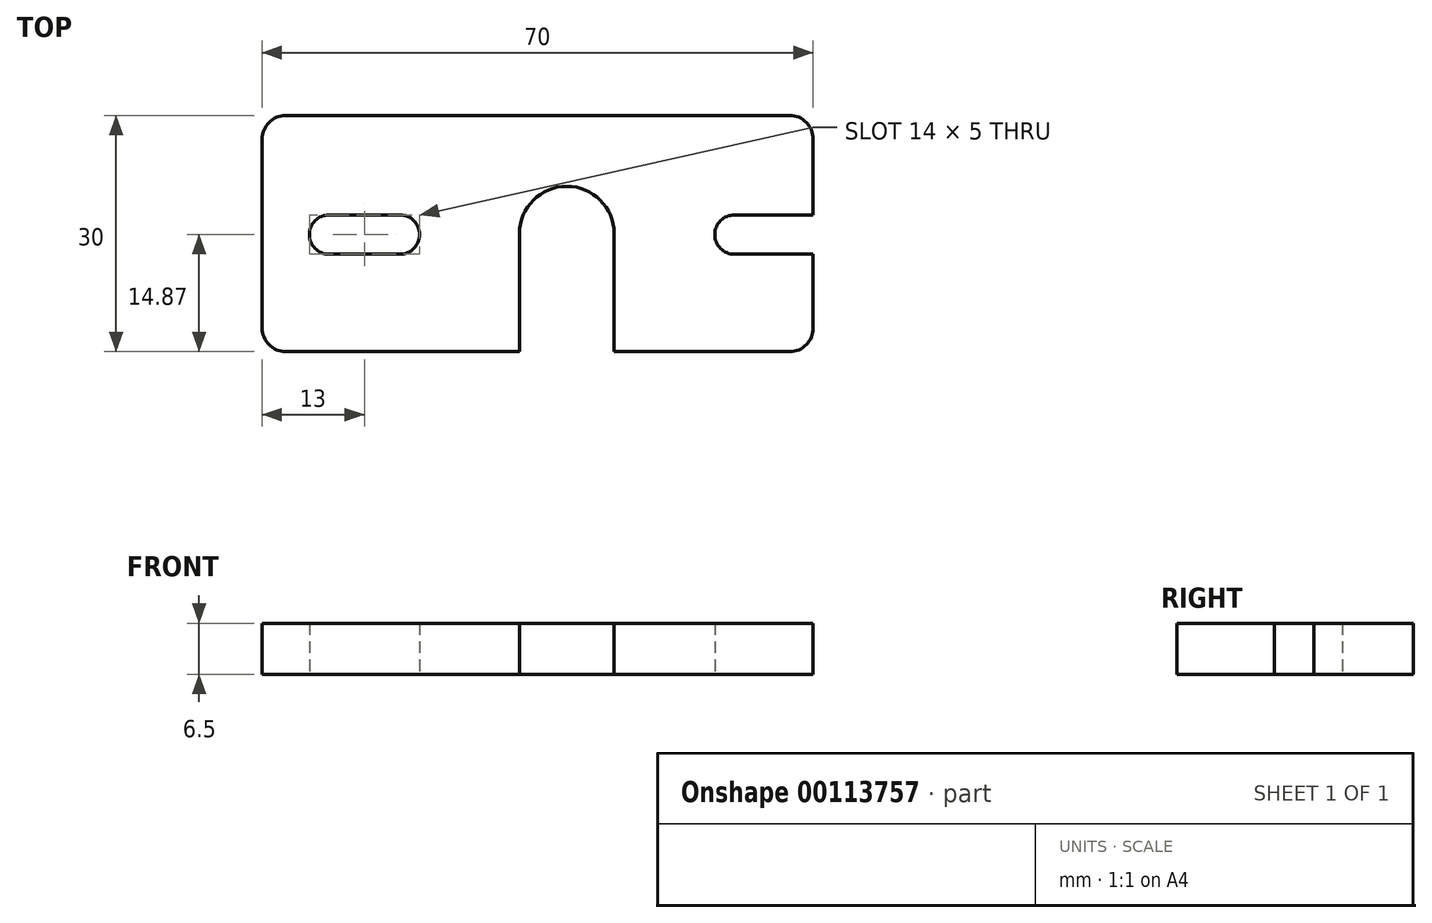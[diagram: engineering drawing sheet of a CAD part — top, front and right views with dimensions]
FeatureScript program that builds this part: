
annotation { "Feature Type Name" : "Feature", "Feature Type Description" : "" }
export const myFeature = defineFeature(function(context is Context, id is Id, definition is map)
    precondition{}
    {
        {
            var Q0;
            Q0=qCreatedBy(makeId("Top.planeOp"),FACE);
            var sketch = newSketch(context, id + "F0", { "sketchPlane" : qUnion([Q0])});
            skLineSegment(sketch, "E0.bottom", {"start": v(-35.7, 15.13) * mm, "end": v(28.3, 15.13) * mm});
            skLineSegment(sketch, "E0.top", {"start": v(-35.7, -14.87) * mm, "end": v(28.3, -14.87) * mm});
            skLineSegment(sketch, "E0.left", {"start": v(-38.7, 12.13) * mm, "end": v(-38.7, -11.87) * mm});
            skLineSegment(sketch, "E0.right", {"start": v(31.3, 12.13) * mm, "end": v(31.3, -11.87) * mm});
            skLineSegment(sketch, "E1.bottom", {"start": v(6, -14.87) * mm, "end": v(-6, -14.87) * mm});
            skLineSegment(sketch, "E1.top", {"start": v(6, 0.13) * mm, "end": v(-6, 0.13) * mm});
            skLineSegment(sketch, "E1.left", {"start": v(6, -14.87) * mm, "end": v(6, 0.13) * mm});
            skLineSegment(sketch, "E1.right", {"start": v(-6, -14.87) * mm, "end": v(-6, 0.13) * mm});
            skArc(sketch, "E2", {"start": v(6, 0.13) * mm, "mid": v(0, 6.13) * mm, "end": v(-6, 0.13) * mm});
            skPoint(sketch, "E3.visualSharp", {"position": v(-38.7, 15.13) * mm});
            skArc(sketch, "E3.filletArc", {"start": v(-35.7, 15.13) * mm, "mid": v(-37.82, 14.25) * mm, "end": v(-38.7, 12.13) * mm});
            skPoint(sketch, "E4.visualSharp", {"position": v(31.3, 15.13) * mm});
            skArc(sketch, "E4.filletArc", {"start": v(31.3, 12.13) * mm, "mid": v(30.42, 14.25) * mm, "end": v(28.3, 15.13) * mm});
            skPoint(sketch, "E5.visualSharp", {"position": v(31.3, -14.87) * mm});
            skArc(sketch, "E5.filletArc", {"start": v(28.3, -14.87) * mm, "mid": v(30.42, -13.99) * mm, "end": v(31.3, -11.87) * mm});
            skPoint(sketch, "E6.visualSharp", {"position": v(-38.7, -14.87) * mm});
            skArc(sketch, "E6.filletArc", {"start": v(-38.7, -11.87) * mm, "mid": v(-37.82, -13.99) * mm, "end": v(-35.7, -14.87) * mm});
            skLineSegment(sketch, "E7.bottom", {"start": v(21.3, 2.5) * mm, "end": v(31.3, 2.5) * mm});
            skLineSegment(sketch, "E7.top", {"start": v(21.3, -2.5) * mm, "end": v(31.3, -2.5) * mm});
            skLineSegment(sketch, "E7.left", {"start": v(21.3, 2.5) * mm, "end": v(21.3, -2.5) * mm});
            skLineSegment(sketch, "E7.right", {"start": v(31.3, 2.5) * mm, "end": v(31.3, -2.5) * mm});
            skArc(sketch, "E8", {"start": v(21.3, 2.5) * mm, "mid": v(18.8, 0) * mm, "end": v(21.3, -2.5) * mm});
            skLineSegment(sketch, "E9.bottom", {"start": v(-30.2, 2.5) * mm, "end": v(-21.2, 2.5) * mm});
            skLineSegment(sketch, "E9.top", {"start": v(-30.2, -2.5) * mm, "end": v(-21.2, -2.5) * mm});
            skLineSegment(sketch, "E9.left", {"start": v(-30.2, 2.5) * mm, "end": v(-30.2, -2.5) * mm});
            skLineSegment(sketch, "E9.right", {"start": v(-21.2, 2.5) * mm, "end": v(-21.2, -2.5) * mm});
            skArc(sketch, "E10", {"start": v(-21.2, -2.5) * mm, "mid": v(-18.7, 0) * mm, "end": v(-21.2, 2.5) * mm});
            skArc(sketch, "E11", {"start": v(-30.2, 2.5) * mm, "mid": v(-32.7, 0) * mm, "end": v(-30.2, -2.5) * mm});
            skSolve(sketch);
        }
        {
            var Q0;
            Q0=makeQuery(id+"F0.imprint","IMPRINT",FACE,{"disambiguationData":[TD([[makeQuery(id+"F0.imprint","IMPRINT",EDGE,{"derivedFrom":sQuery(id+"F0.wireOp",EDGE,"E0.bottom")}),-1.0]])]});
            extrude(context, id + "F1", {"entities" : qUnion([Q0]), "depth" : 6.5 * mm});
        }
    });
